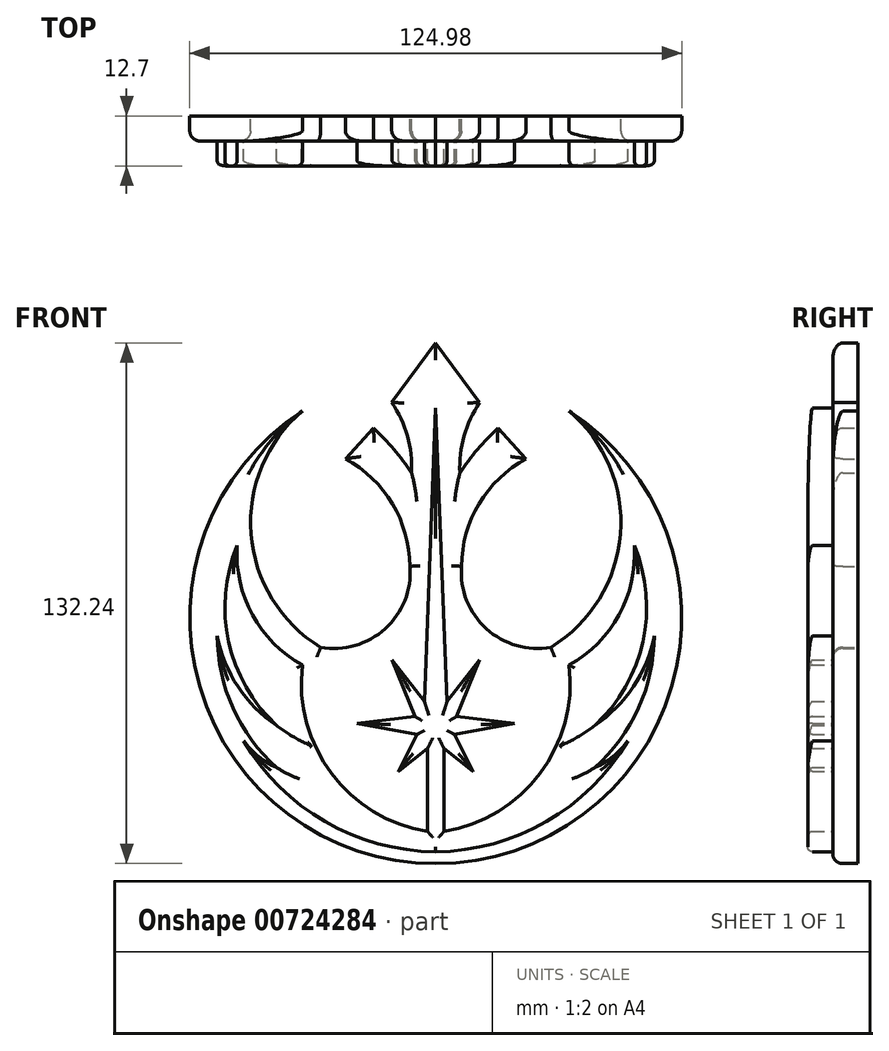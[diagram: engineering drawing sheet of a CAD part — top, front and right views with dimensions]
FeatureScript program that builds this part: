
annotation { "Feature Type Name" : "Feature", "Feature Type Description" : "" }
export const myFeature = defineFeature(function(context is Context, id is Id, definition is map)
    precondition{}
    {
        {
            var Q0;
            Q0=qCreatedBy(makeId("Front.planeOp"),FACE);
            var sketch = newSketch(context, id + "F0", { "sketchPlane" : qUnion([Q0])});
            skArc(sketch, "E0", {"start": v(-33.86, 48.96) * mm, "mid": v(0, -66.04) * mm, "end": v(33.86, 48.96) * mm});
            skArc(sketch, "E1", {"start": v(-50.46, 14.73) * mm, "mid": v(-46.55, -2.84) * mm, "end": v(-33.89, -15.62) * mm});
            skArc(sketch, "E2", {"start": v(-50.46, 14.73) * mm, "mid": v(-52.63, -9.7) * mm, "end": v(-40.4, -30.96) * mm});
            skArc(sketch, "E3", {"start": v(-55.5, -8.17) * mm, "mid": v(-50.25, -21.09) * mm, "end": v(-40.4, -30.96) * mm});
            skArc(sketch, "E4", {"start": v(-55.5, -8.17) * mm, "mid": v(-51.51, -26.53) * mm, "end": v(-40.4, -41.68) * mm});
            skArc(sketch, "E5", {"start": v(-48.78, -34.85) * mm, "mid": v(-45.05, -38.83) * mm, "end": v(-40.4, -41.68) * mm});
            skArc(sketch, "E6", {"start": v(-48.78, -34.85) * mm, "mid": v(-28.1, -55.38) * mm, "end": v(0, -63.06) * mm});
            skArc(sketch, "E7", {"start": v(-33.89, -15.62) * mm, "mid": v(-26.45, -43.16) * mm, "end": v(-2.05, -57.92) * mm});
            skArc(sketch, "E8", {"start": v(-6.13, 33.22) * mm, "mid": v(-7.19, 42.56) * mm, "end": v(-11.18, 51.08) * mm});
            skArc(sketch, "E9", {"start": v(-6.13, 33.22) * mm, "mid": v(-10.63, 39.17) * mm, "end": v(-15.8, 44.56) * mm});
            skArc(sketch, "E10", {"start": v(-33.86, 48.96) * mm, "mid": v(-46.93, 17.74) * mm, "end": v(-29.24, -11.1) * mm});
            skArc(sketch, "E11", {"start": v(-29.24, -11.1) * mm, "mid": v(-12.85, -6.38) * mm, "end": v(-6.55, 9.48) * mm});
            skArc(sketch, "E12", {"start": v(-6.55, 9.48) * mm, "mid": v(-11.02, 25.37) * mm, "end": v(-22.94, 36.8) * mm});
            skLineSegment(sketch, "E13", {"start": v(-22.94, 36.8) * mm, "end": v(-15.8, 44.56) * mm});
            skLineSegment(sketch, "E14", {"start": v(-11.18, 51.08) * mm, "end": v(0, 66.2) * mm});
            skLineSegment(sketch, "E15", {"start": v(-2.05, -57.92) * mm, "end": v(-2.05, -36.74) * mm});
            skLineSegment(sketch, "E16", {"start": v(-2.05, -36.74) * mm, "end": v(-9.5, -42.62) * mm});
            skLineSegment(sketch, "E17", {"start": v(-9.5, -42.62) * mm, "end": v(-4.77, -33.22) * mm});
            skLineSegment(sketch, "E18", {"start": v(-4.77, -33.22) * mm, "end": v(-20, -30.44) * mm});
            skLineSegment(sketch, "E19", {"start": v(-20, -30.44) * mm, "end": v(-5.24, -28.71) * mm});
            skLineSegment(sketch, "E20", {"start": v(-5.24, -28.71) * mm, "end": v(-11.07, -14.31) * mm});
            skLineSegment(sketch, "E21", {"start": v(-11.07, -14.31) * mm, "end": v(-2.86, -24.91) * mm});
            skLineSegment(sketch, "E22", {"start": v(-2.86, -24.91) * mm, "end": v(0, 49.68) * mm});
            skLineSegment(sketch, "E23.MirrorCS", {"start": v(11.18, 51.08) * mm, "end": v(0, 66.2) * mm});
            skArc(sketch, "E24.MirrorCS", {"start": v(6.13, 33.22) * mm, "mid": v(10.63, 39.17) * mm, "end": v(15.8, 44.56) * mm});
            skLineSegment(sketch, "E25.MirrorCS", {"start": v(22.94, 36.8) * mm, "end": v(15.8, 44.56) * mm});
            skArc(sketch, "E26.MirrorCS", {"start": v(6.55, 9.48) * mm, "mid": v(11.02, 25.37) * mm, "end": v(22.94, 36.8) * mm});
            skArc(sketch, "E27.MirrorCS", {"start": v(29.24, -11.1) * mm, "mid": v(12.85, -6.38) * mm, "end": v(6.55, 9.48) * mm});
            skArc(sketch, "E28.MirrorCS", {"start": v(33.86, 48.96) * mm, "mid": v(46.93, 17.74) * mm, "end": v(29.24, -11.1) * mm});
            skArc(sketch, "E29.MirrorCS", {"start": v(50.46, 14.73) * mm, "mid": v(46.55, -2.84) * mm, "end": v(33.89, -15.62) * mm});
            skArc(sketch, "E30.MirrorCS", {"start": v(50.46, 14.73) * mm, "mid": v(52.63, -9.7) * mm, "end": v(40.4, -30.96) * mm});
            skArc(sketch, "E31.MirrorCS", {"start": v(55.5, -8.17) * mm, "mid": v(50.25, -21.09) * mm, "end": v(40.4, -30.96) * mm});
            skArc(sketch, "E32.MirrorCS", {"start": v(55.5, -8.17) * mm, "mid": v(51.51, -26.53) * mm, "end": v(40.4, -41.68) * mm});
            skArc(sketch, "E33.MirrorCS", {"start": v(48.78, -34.85) * mm, "mid": v(45.05, -38.83) * mm, "end": v(40.4, -41.68) * mm});
            skArc(sketch, "E34.MirrorCS", {"start": v(48.78, -34.85) * mm, "mid": v(28.1, -55.38) * mm, "end": v(0, -63.06) * mm});
            skLineSegment(sketch, "E35.MirrorCS", {"start": v(2.05, -57.92) * mm, "end": v(2.05, -36.74) * mm});
            skLineSegment(sketch, "E36.MirrorCS", {"start": v(2.05, -36.74) * mm, "end": v(9.5, -42.62) * mm});
            skLineSegment(sketch, "E37.MirrorCS", {"start": v(9.5, -42.62) * mm, "end": v(4.77, -33.22) * mm});
            skLineSegment(sketch, "E38.MirrorCS", {"start": v(4.77, -33.22) * mm, "end": v(20, -30.44) * mm});
            skLineSegment(sketch, "E39.MirrorCS", {"start": v(20, -30.44) * mm, "end": v(5.24, -28.71) * mm});
            skLineSegment(sketch, "E40.MirrorCS", {"start": v(5.24, -28.71) * mm, "end": v(11.07, -14.31) * mm});
            skLineSegment(sketch, "E41.MirrorCS", {"start": v(11.07, -14.31) * mm, "end": v(2.86, -24.91) * mm});
            skLineSegment(sketch, "E42.MirrorCS", {"start": v(2.86, -24.91) * mm, "end": v(0, 49.68) * mm});
            skArc(sketch, "E43.MirrorCS", {"start": v(6.13, 33.22) * mm, "mid": v(7.19, 42.56) * mm, "end": v(11.18, 51.08) * mm});
            skArc(sketch, "E44.MirrorCS", {"start": v(33.89, -15.62) * mm, "mid": v(26.45, -43.16) * mm, "end": v(2.05, -57.92) * mm});
            skSolve(sketch);
        }
        {
            var Q0;
            Q0=makeQuery(id+"F0.imprint","IMPRINT",FACE,{"disambiguationData":[TD([[makeQuery(id+"F0.imprint","IMPRINT",EDGE,{"derivedFrom":sQuery(id+"F0.wireOp",EDGE,"E1")}),-1.0]])]});
            extrude(context, id + "F1", {"entities" : qUnion([Q0]), "depth" : 12.7 * mm, "offsetDistance" : 25.4 * mm});
        }
        {
            var Q0;
            Q0=makeQuery(id+"F0.imprint","IMPRINT",FACE,{"disambiguationData":[TD([[makeQuery(id+"F0.imprint","IMPRINT",EDGE,{"derivedFrom":sQuery(id+"F0.wireOp",EDGE,"E0")}),1.0]])]});
            extrude(context, id + "F2", {"entities" : qUnion([Q0]), "operationType" : NewBodyOperationType.ADD, "depth" : 6.35 * mm, "offsetDistance" : 25.4 * mm});
        }
        {
            var Q0;
            Q0=makeQuery(id+"F2.opExtrude","CAP_EDGE",EDGE,{"disambiguationData":[OSD([sQuery(id+"F0.wireOp",EDGE,"E28.MirrorCS")])],"isStart":false});
            var Q1;
            Q1=makeQuery(id+"F2.opExtrude","CAP_EDGE",EDGE,{"disambiguationData":[OSD([sQuery(id+"F0.wireOp",EDGE,"E27.MirrorCS")])],"isStart":false});
            var Q2;
            Q2=makeQuery(id+"F2.opExtrude","CAP_EDGE",EDGE,{"disambiguationData":[OSD([sQuery(id+"F0.wireOp",EDGE,"E26.MirrorCS")])],"isStart":false});
            var Q3;
            Q3=makeQuery(id+"F2.opExtrude","CAP_EDGE",EDGE,{"disambiguationData":[OSD([sQuery(id+"F0.wireOp",EDGE,"E12")])],"isStart":false});
            var Q4;
            Q4=makeQuery(id+"F2.opExtrude","CAP_EDGE",EDGE,{"disambiguationData":[OSD([sQuery(id+"F0.wireOp",EDGE,"E11")])],"isStart":false});
            var Q5;
            Q5=makeQuery(id+"F2.opExtrude","CAP_EDGE",EDGE,{"disambiguationData":[OSD([sQuery(id+"F0.wireOp",EDGE,"E10")])],"isStart":false});
            var Q6;
            Q6=makeQuery(id+"F2.opExtrude","CAP_EDGE",EDGE,{"disambiguationData":[OSD([sQuery(id+"F0.wireOp",EDGE,"E25.MirrorCS")])],"isStart":false});
            var Q7;
            Q7=makeQuery(id+"F2.opExtrude","CAP_EDGE",EDGE,{"disambiguationData":[OSD([sQuery(id+"F0.wireOp",EDGE,"E24.MirrorCS")])],"isStart":false});
            var Q8;
            Q8=makeQuery(id+"F2.opExtrude","CAP_EDGE",EDGE,{"disambiguationData":[OSD([sQuery(id+"F0.wireOp",EDGE,"E43.MirrorCS")])],"isStart":false});
            var Q9;
            Q9=makeQuery(id+"F2.opExtrude","CAP_EDGE",EDGE,{"disambiguationData":[OSD([sQuery(id+"F0.wireOp",EDGE,"E23.MirrorCS")])],"isStart":false});
            var Q10;
            Q10=makeQuery(id+"F2.opExtrude","CAP_EDGE",EDGE,{"disambiguationData":[OSD([sQuery(id+"F0.wireOp",EDGE,"E14")])],"isStart":false});
            var Q11;
            Q11=makeQuery(id+"F2.opExtrude","CAP_EDGE",EDGE,{"disambiguationData":[OSD([sQuery(id+"F0.wireOp",EDGE,"E9")])],"isStart":false});
            var Q12;
            Q12=makeQuery(id+"F2.opExtrude","CAP_EDGE",EDGE,{"disambiguationData":[OSD([sQuery(id+"F0.wireOp",EDGE,"E8")])],"isStart":false});
            var Q13;
            Q13=makeQuery(id+"F2.opExtrude","CAP_EDGE",EDGE,{"disambiguationData":[OSD([sQuery(id+"F0.wireOp",EDGE,"E13")])],"isStart":false});
            var Q14;
            Q14=makeQuery(id+"F2.opExtrude","CAP_EDGE",EDGE,{"disambiguationData":[OSD([sQuery(id+"F0.wireOp",EDGE,"E0")])],"isStart":false});
            fillet(context, id + "F3", {"entities" : qUnion([Q0, Q1, Q2, Q3, Q4, Q5, Q6, Q7, Q8, Q9, Q10, Q11, Q12, Q13, Q14]), "radius" : 2.54 * mm, "tangentPropagation" : true, "allowEdgeOverflow" : false});
        }
        {
            var Q0;
            Q0=makeQuery(id+"F1.opExtrude","CAP_FACE",FACE,{"disambiguationData":[OSD([sQuery(id+"F0.wireOp",EDGE,"E1"),sQuery(id+"F0.wireOp",EDGE,"E2"),sQuery(id+"F0.wireOp",EDGE,"E3"),sQuery(id+"F0.wireOp",EDGE,"E4"),sQuery(id+"F0.wireOp",EDGE,"E5"),sQuery(id+"F0.wireOp",EDGE,"E6"),sQuery(id+"F0.wireOp",EDGE,"E7"),sQuery(id+"F0.wireOp",EDGE,"E15"),sQuery(id+"F0.wireOp",EDGE,"E16"),sQuery(id+"F0.wireOp",EDGE,"E17"),sQuery(id+"F0.wireOp",EDGE,"E18"),sQuery(id+"F0.wireOp",EDGE,"E19"),sQuery(id+"F0.wireOp",EDGE,"E20"),sQuery(id+"F0.wireOp",EDGE,"E21"),sQuery(id+"F0.wireOp",EDGE,"E22"),sQuery(id+"F0.wireOp",EDGE,"E29.MirrorCS"),sQuery(id+"F0.wireOp",EDGE,"E30.MirrorCS"),sQuery(id+"F0.wireOp",EDGE,"E31.MirrorCS"),sQuery(id+"F0.wireOp",EDGE,"E32.MirrorCS"),sQuery(id+"F0.wireOp",EDGE,"E33.MirrorCS"),sQuery(id+"F0.wireOp",EDGE,"E34.MirrorCS"),sQuery(id+"F0.wireOp",EDGE,"E35.MirrorCS"),sQuery(id+"F0.wireOp",EDGE,"E36.MirrorCS"),sQuery(id+"F0.wireOp",EDGE,"E37.MirrorCS"),sQuery(id+"F0.wireOp",EDGE,"E38.MirrorCS"),sQuery(id+"F0.wireOp",EDGE,"E39.MirrorCS"),sQuery(id+"F0.wireOp",EDGE,"E40.MirrorCS"),sQuery(id+"F0.wireOp",EDGE,"E41.MirrorCS"),sQuery(id+"F0.wireOp",EDGE,"E42.MirrorCS"),sQuery(id+"F0.wireOp",EDGE,"E44.MirrorCS")])],"isStart":false});
            fillet(context, id + "F4", {"entities" : qUnion([Q0]), "radius" : 1.27 * mm, "tangentPropagation" : true, "allowEdgeOverflow" : false});
        }
    });
